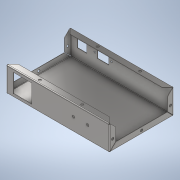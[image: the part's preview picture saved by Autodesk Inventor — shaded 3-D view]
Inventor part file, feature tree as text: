
AUTODESK INVENTOR PART (.ipt)
format: ipt  version: 2020.3 (Build 243373000, 373)  size: 315,392 bytes
history: native  units: mm
features: sketch x8, sheet_metal_op x7, other x4, hole x3, extrude x2
ambient origin geometry x8: Origin, YZ Plane, XZ Plane, XY Plane, X Axis, Y Axis, Z Axis, Center Point
bodies: Solid1 (feature_tree)
feature tree (24):
  sheet_metal_op  "Face1"
  sheet_metal_op  "Flange1"
  sheet_metal_op  "Flange2"
  other  "Corner Chamfer2"
  hole  "Hole1"  [1 undecoded]
  hole  "Hole2"  [1 undecoded]
  extrude  "Extrusion1"  Depth=2.0mm
  extrude  "Extrusion2"  Depth=1.0mm TaperAngle=90.0deg
  hole  "Hole4"  [1 undecoded]
  sketch  "Sketch1"  dims[d0=248.0mm d1=155.0mm]
  other  "Plate1"
  sketch  "Sketch2"  dims[d2=1.0mm d3=1.0mm]
  other  "Plate2"
  sheet_metal_op  "Bend1"
  sheet_metal_op  "Corner1"
  sketch  "Sketch3"  dims[d4=0.5mm d5=2.0mm]
  other  "Plate3"
  sheet_metal_op  "Bend2"
  sheet_metal_op  "Corner2"
  sketch  "Sketch6"  dims[d6=1.0mm d7=60.0mm d8=90.0deg d9=1.0mm]
  sketch  "Sketch7"  dims[d10=4.0mm d11=1.0mm]
  sketch  "Sketch8"  dims[d12=1.0mm]
  sketch  "Sketch10"  dims[d13=1.0mm]
  sketch  "Sketch11"  dims[d14=0.5mm d15=2.0mm d16=1.0mm d17=15.0mm d18=90.0deg d19=1.0mm d20=4.0mm d21=1.0mm d22=1.0mm d26=12.0mm d27=6.0mm d28=45.0deg d53=8.0mm d54=72.0mm d55=72.0mm d56=8.0mm d57=6.0mm d58=6.0mm d59=4.0mm d60=2.0mm d61=90.0deg d62=1.0mm d63=20.594885mm d64=8.0mm d65=8.0mm d66=8.0mm d67=77.5mm d68=25.0mm d69=6.0mm d70=6.0mm d71=4.0mm d72=2.0mm d73=90.0deg d74=1.0mm d75=20.594885mm d76=44.3mm d77=44.3mm d78=15.0mm d79=5.85mm d80=5.85mm d81=10.0mm d82=0.0mm d93=23.0mm d94=27.0mm d95=15.0mm d96=5.0mm d97=28.0mm d98=20.0mm d99=10.0mm d100=25.0mm d101=4.0mm d102=10.0mm d103=6.1mm d104=4.0mm d105=40.2mm d106=10.0mm d107=0.0mm d108=30.0mm d109=52.0mm d110=34.0mm d111=6.0mm d112=6.0mm d113=4.0mm d114=2.0mm d115=90.0deg d116=1.0mm d117=20.594885mm]
note: 3 required parameter values undecoded (feature->parameter linkage not recoverable at this tier; creation-order binding heuristic only, values carry confidence <= 0.55)
